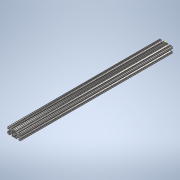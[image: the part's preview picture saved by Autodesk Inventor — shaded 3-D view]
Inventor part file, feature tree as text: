
AUTODESK INVENTOR PART (.ipt)
format: ipt  version: 2020 (Build 240168000, 168)  size: 353,280 bytes
history: native  units: in
note: dims shown in document units (in); Inventor stores cm internally (conversion verified against a paired STEP export)
features: sketch x2, extrude x1
ambient origin geometry x8: Origin, YZ Plane, XZ Plane, XY Plane, X Axis, Y Axis, Z Axis, Center Point
bodies: Solid1 (feature_tree)
feature tree (3):
  extrude  "Extrusion1"  [1 undecoded]
  sketch  "Sketch2"
  sketch  "Sketch1"  dims[d0=23.0in d1=0.0in]
note: 1 required parameter value undecoded (feature->parameter linkage not recoverable at this tier; creation-order binding heuristic only, values carry confidence <= 0.55)
